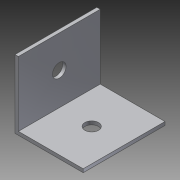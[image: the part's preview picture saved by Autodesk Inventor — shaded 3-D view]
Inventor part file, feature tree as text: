
AUTODESK INVENTOR PART (.ipt)
format: ipt  version: 2014 SP1 (Build 180222100, 222)  size: 93,696 bytes
history: native  units: in
note: dims shown in document units (in); Inventor stores cm internally (conversion verified against a paired STEP export)
features: extrude x3, sketch x3
ambient origin geometry x8: Origin, YZ Plane, XZ Plane, XY Plane, X Axis, Y Axis, Z Axis, Center Point
bodies: Solid1 (feature_tree)
feature tree (6):
  extrude  "Extrusion1"  Depth=0.0312in
  sketch  "Sketch2"  dims[d2=0.75in d3=0.0in d4=0.125in]
  sketch  "Sketch3"  dims[d5=0.125in d6=0.75in d7=0.0in d8=0.75in d9=0.0in]
  extrude  "Extrusion2"  Depth=0.75in
  extrude  "Extrusion3"  Depth=0.75in TaperAngle=0.0deg
  sketch  "Sketch1"  dims[d0=0.625in d1=0.0312in]
